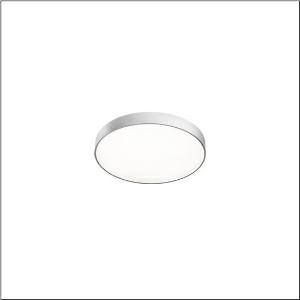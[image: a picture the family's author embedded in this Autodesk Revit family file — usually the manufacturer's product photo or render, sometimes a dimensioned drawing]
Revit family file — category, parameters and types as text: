
# Revit family: round_21_s_51mr34gd0421s
name_source: partatom
category: Lighting Fixtures
units: mm (PartAtom-declared; Revit-internal decimal feet)

## family parameters
Cut with Voids When Loaded = No
Host = Face
Light Source = No
Part Type = Normal
Room Calculation Point = No
Round Connector Dimension = Use Diameter
Shared = No

## types (1)
- Round 21 S (1 x LED, 4090 lm, 28.3 W, 4000K)
    Apparent Load = 28 VA
    CIE Flux Codes = 49 80 96 79 100
    Color Rendering = 80
    Color Temperature = 4000K
    Default Elevation = 1800 mm
    Description = Round 21 S, wall and ceiling luminaire, primary optical cover: cover, of PMMA, opal, light emission: direct/indirect distribution, primary light characteristic: symmetric, installation type: suspended mounting, surface-mounted, LED, rated luminous flux: 4.090lm, luminous efficacy: 135lm/W, light colour: 840, colour temperature: 4000K, control gear: DALI 2, with terminal, 5-pole, mains connection: 230V, AC, 50/60Hz, rated input power: 28.3W, housing, of aluminium, coated, silver, diameter: 400mm, height: 62mm, protection rating (complete): IP40, insulation class (complete): insulation class I (protective earthing), certification: CE, impact resistance: IK04, permissible operating ambient temperature: -10..+35°C, packaging unit: 1 piece
    Height = 87 mm
    Lamp = 1 x LED
    Lamp Light Flux = 4090 lm
    Lamp Power = 28.3 W
    Lamp count = 1
    Length = 400 mm
    Luminous efficacy = 145 lm/W
    Manufacturer = Siteco
    ModVariant = No
    Model = 51MR34GD0421S
    Mounting Place = Wall
    Mounting Type = Surface mounted
    Number of Poles = 1
    OnlyDefault = Yes
    Power Factor = 1
    Product Name = Round 21 S
    Product group = wall and ceiling luminaire
    ProductGroupID = 2001
    Protection Class = Protection class I
    Protection Degree = IP 40
    RLX_Detail_Level = 1
    RLX_Emergency_Light_Flux = 0 lm
    RLX_Emergency_Type = 0
    RLX_Emergency_Type_DB = No
    RlxData = <blob elided: 11573 chars, md5=2a5ea558>
    Socket = socket
    Standby Power = 0 W
    System Light Flux = 4090 lm
    System Power = 28 W
    Type Comments = Product without accessories
    Type Image = l_1258309.jpg
    URL = http://relux.com
    VarID = ---
    Voltage = 0 V
    Weight = 0.00 kg
    Width = 0 mm  [stored 0 ft]

note: [stored X ft] marks values corroborated as IEEE doubles in the binary element streams (Revit-internal decimal feet)

## geometry (parser evidence)
native form markers: Sweep x12
no freeform markers — native parametric forms only
